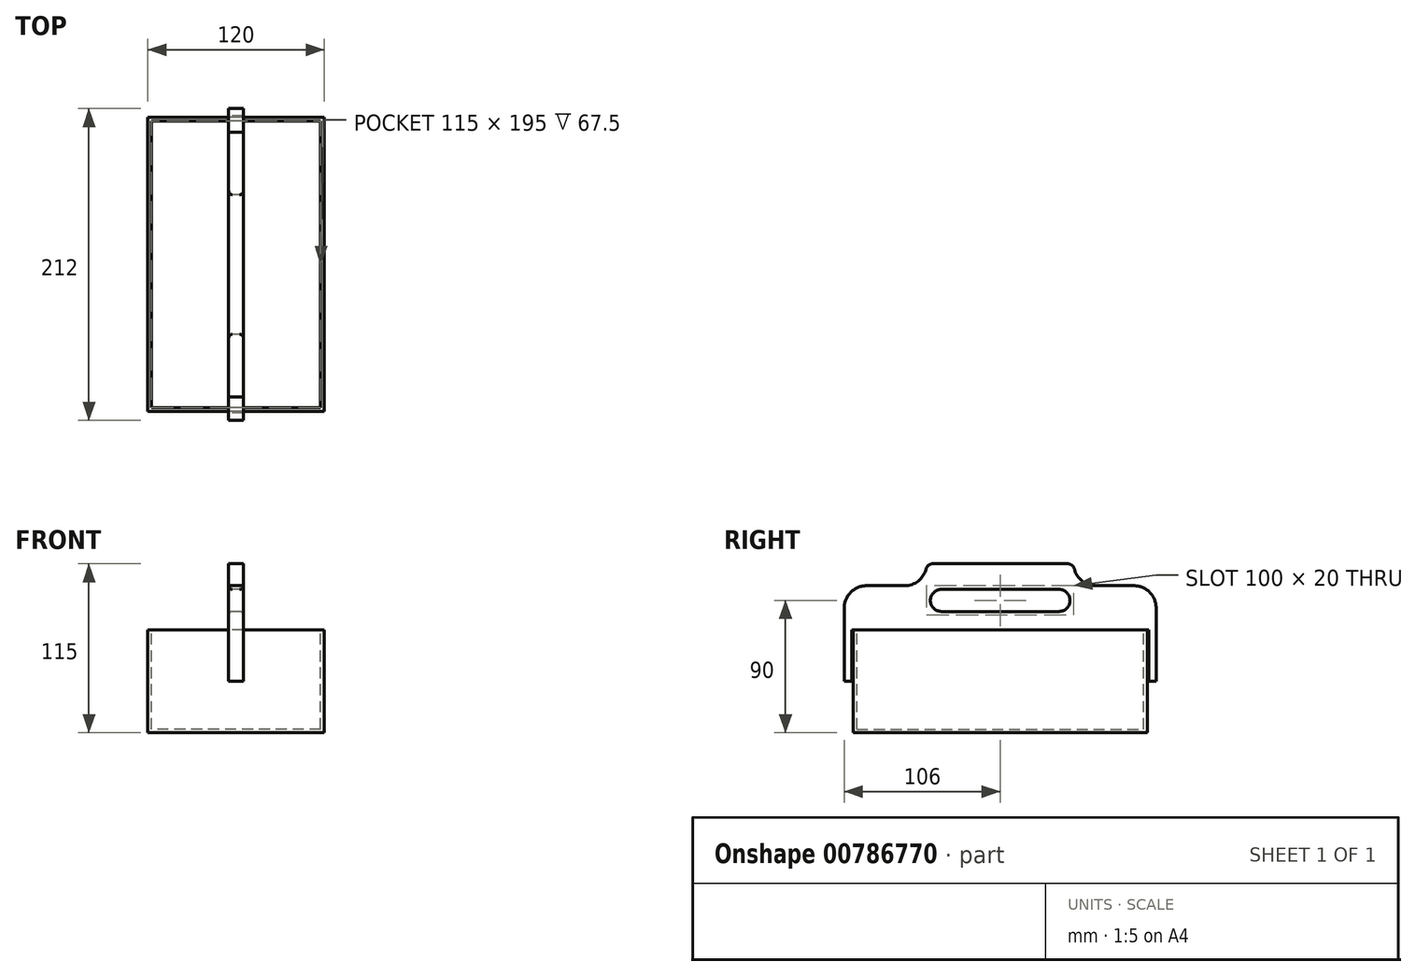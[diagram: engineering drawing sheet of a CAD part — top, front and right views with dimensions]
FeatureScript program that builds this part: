
annotation { "Feature Type Name" : "Feature", "Feature Type Description" : "" }
export const myFeature = defineFeature(function(context is Context, id is Id, definition is map)
    precondition{}
    {
        {
            var Q0;
            Q0=qCreatedBy(makeId("Front.planeOp"),FACE);
            var sketch = newSketch(context, id + "F0", { "sketchPlane" : qUnion([Q0])});
            skPoint(sketch, "E0.middle", {"position": v(0, 0) * mm});
            skLineSegment(sketch, "E1.bottom", {"start": v(60, -35) * mm, "end": v(-60, -35) * mm});
            skLineSegment(sketch, "E1.top", {"start": v(60, 35) * mm, "end": v(-60, 35) * mm});
            skLineSegment(sketch, "E1.left", {"start": v(60, -35) * mm, "end": v(60, 35) * mm});
            skLineSegment(sketch, "E1.right", {"start": v(-60, -35) * mm, "end": v(-60, 35) * mm});
            skSolve(sketch);
        }
        {
            var Q0;
            Q0 = qSketchRegion(id + "F0", true);
            extrude(context, id + "F1", {"entities" : qUnion([Q0]), "endBound" : BoundingType.SYMMETRIC, "depth" : 200 * mm, "offsetDistance" : 25 * mm});
        }
        {
            var Q0;
            Q0=makeQuery(id+"F1.opExtrude","SWEPT_FACE",FACE,{"disambiguationData":[OSD([sQuery(id+"F0.wireOp",EDGE,"E1.top")])]});
            shell(context, id + "F2", {"entities" : qUnion([Q0]), "thickness" : 2.5 * mm});
        }
        {
            var Q0;
            Q0=qCreatedBy(makeId("Right.planeOp"),FACE);
            var sketch = newSketch(context, id + "F3", { "sketchPlane" : qUnion([Q0])});
            skLineSegment(sketch, "E2", {"start": v(-100, 0) * mm, "end": v(-100, 35) * mm});
            skLineSegment(sketch, "E3", {"start": v(101, 35) * mm, "end": v(101, 0) * mm});
            skLineSegment(sketch, "E4", {"start": v(101, 0) * mm, "end": v(106, 0) * mm});
            skLineSegment(sketch, "E5", {"start": v(106, 0) * mm, "end": v(106, 50) * mm});
            skLineSegment(sketch, "E6", {"start": v(-101, 35) * mm, "end": v(-101, 0) * mm});
            skLineSegment(sketch, "E7", {"start": v(-101, 0) * mm, "end": v(-106, 0) * mm});
            skLineSegment(sketch, "E8", {"start": v(-106, 0) * mm, "end": v(-106, 50) * mm});
            skLineSegment(sketch, "E9", {"start": v(0, 80) * mm, "end": v(45.64, 80) * mm});
            skLineSegment(sketch, "E10", {"start": v(50, 80) * mm, "end": v(-45.64, 80) * mm});
            skLineSegment(sketch, "E11", {"start": v(90, 65) * mm, "end": v(90, 50) * mm});
            skArc(sketch, "E12", {"start": v(106, 50) * mm, "mid": v(101.26, 60.98) * mm, "end": v(90, 65) * mm});
            skArc(sketch, "E13", {"start": v(-90, 65) * mm, "mid": v(-101.26, 60.98) * mm, "end": v(-106, 50) * mm});
            skArc(sketch, "E14", {"start": v(-65, 65) * mm, "mid": v(-55.81, 68.14) * mm, "end": v(-50.48, 76.25) * mm});
            skPoint(sketch, "E15.visualSharp", {"position": v(-50, 80) * mm});
            skArc(sketch, "E15.filletArc", {"start": v(-45.64, 80) * mm, "mid": v(-48.7, 78.95) * mm, "end": v(-50.48, 76.25) * mm});
            skArc(sketch, "E16", {"start": v(50.48, 76.25) * mm, "mid": v(55.81, 68.14) * mm, "end": v(65, 65) * mm});
            skPoint(sketch, "E17.visualSharp", {"position": v(50, 80) * mm});
            skArc(sketch, "E17.filletArc", {"start": v(50.48, 76.25) * mm, "mid": v(48.7, 78.95) * mm, "end": v(45.64, 80) * mm});
            skLineSegment(sketch, "E18", {"start": v(-90, 65) * mm, "end": v(-65, 65) * mm});
            skLineSegment(sketch, "E19", {"start": v(65, 65) * mm, "end": v(90, 65) * mm});
            skLineSegment(sketch, "E20", {"start": v(0, 35) * mm, "end": v(0, 47.5) * mm});
            skLineSegment(sketch, "E21", {"start": v(40, 47.5) * mm, "end": v(-40, 47.5) * mm});
            skLineSegment(sketch, "E22", {"start": v(0, 47.5) * mm, "end": v(0, 62.5) * mm});
            skArc(sketch, "E23", {"start": v(-40, 62.5) * mm, "mid": v(-47.5, 55) * mm, "end": v(-40, 47.5) * mm});
            skArc(sketch, "E24", {"start": v(40, 47.5) * mm, "mid": v(47.5, 55) * mm, "end": v(40, 62.5) * mm});
            skLineSegment(sketch, "E25", {"start": v(101, 35) * mm, "end": v(-101, 35) * mm});
            skLineSegment(sketch, "E26", {"start": v(-40, 62.5) * mm, "end": v(40, 62.5) * mm});
            skLineSegment(sketch, "E27", {"start": v(0, 0) * mm, "end": v(0, 35) * mm});
            skSolve(sketch);
        }
        {
            var Q0;
            Q0 = qSketchRegion(id + "F3", true);
            extrude(context, id + "F4", {"entities" : qUnion([Q0]), "operationType" : NewBodyOperationType.ADD, "endBound" : BoundingType.SYMMETRIC, "depth" : 10 * mm, "offsetDistance" : 25 * mm});
        }
        {
            var Q0;
            Q0=makeQuery(id+"F4.opExtrude","CAP_EDGE",EDGE,{"disambiguationData":[OSD([sQuery(id+"F3.wireOp",EDGE,"E21")])],"isStart":false});
            var Q1;
            Q1=makeQuery(id+"F4.opExtrude","CAP_EDGE",EDGE,{"disambiguationData":[OSD([sQuery(id+"F3.wireOp",EDGE,"E21")])],"isStart":true});
            fillet(context, id + "F5", {"entities" : qUnion([Q0, Q1]), "tangentPropagation" : true, "radius" : 2.5 * mm, "defaultsChanged" : true, "vertexSettings" : [], "allowEdgeOverflow" : false});
        }
    });
